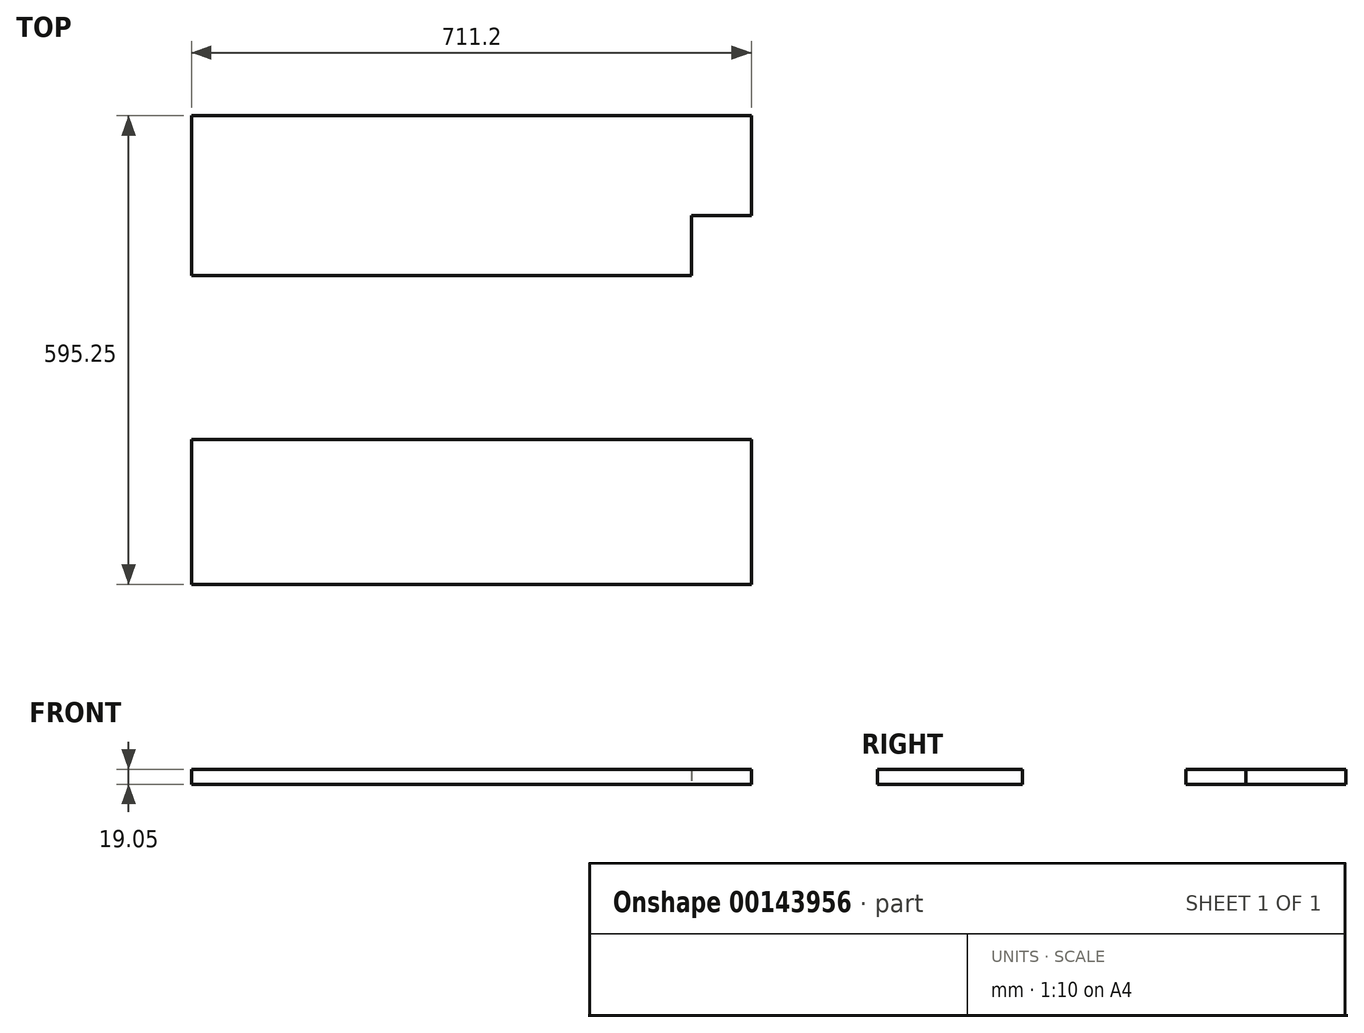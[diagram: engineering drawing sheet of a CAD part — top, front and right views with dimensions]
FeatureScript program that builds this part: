
annotation { "Feature Type Name" : "Feature", "Feature Type Description" : "" }
export const myFeature = defineFeature(function(context is Context, id is Id, definition is map)
    precondition{}
    {
        {
            var Q0;
            Q0=qCreatedBy(makeId("Top.planeOp"),FACE);
            var sketch = newSketch(context, id + "F0", { "sketchPlane" : qUnion([Q0])});
            skLineSegment(sketch, "E0.bottom", {"start": v(-183.98, 99.82) * mm, "end": v(527.22, 99.82) * mm});
            skLineSegment(sketch, "E0.top", {"start": v(-183.98, -103.38) * mm, "end": v(527.22, -103.38) * mm});
            skLineSegment(sketch, "E0.left", {"start": v(-183.98, 99.82) * mm, "end": v(-183.98, -103.38) * mm});
            skLineSegment(sketch, "E0.right", {"start": v(527.22, 99.82) * mm, "end": v(527.22, -103.38) * mm});
            skLineSegment(sketch, "E1", {"start": v(-234.36, 194.25) * mm, "end": v(600.55, 194.25) * mm, "construction": true});
            skLineSegment(sketch, "E2.MirrorCS", {"start": v(-183.98, 288.67) * mm, "end": v(-183.98, 491.87) * mm});
            skLineSegment(sketch, "E3.MirrorCS", {"start": v(-183.98, 288.67) * mm, "end": v(527.22, 288.67) * mm});
            skLineSegment(sketch, "E4.MirrorCS", {"start": v(527.22, 288.67) * mm, "end": v(527.22, 491.87) * mm});
            skLineSegment(sketch, "E5.MirrorCS", {"start": v(-183.98, 491.87) * mm, "end": v(527.22, 491.87) * mm});
            skLineSegment(sketch, "E6.bottom", {"start": v(451.02, 364.87) * mm, "end": v(527.22, 364.87) * mm});
            skLineSegment(sketch, "E6.top", {"start": v(451.02, 288.67) * mm, "end": v(527.22, 288.67) * mm});
            skLineSegment(sketch, "E6.left", {"start": v(451.02, 364.87) * mm, "end": v(451.02, 288.67) * mm});
            skLineSegment(sketch, "E6.right", {"start": v(527.22, 364.87) * mm, "end": v(527.22, 288.67) * mm});
            skSolve(sketch);
        }
        {
            var Q0;
            Q0=makeQuery(id+"F0.imprint","IMPRINT",FACE,{"disambiguationData":[TD([[makeQuery(id+"F0.imprint","IMPRINT",EDGE,{"derivedFrom":sQuery(id+"F0.wireOp",EDGE,"E0.bottom")}),-1.0]])]});
            extrude(context, id + "F1", {"entities" : qUnion([Q0]), "depth" : 19.05 * mm});
        }
        {
            var Q0;
            Q0=makeQuery(id+"F0.imprint","IMPRINT",FACE,{"disambiguationData":[TD([[makeQuery(id+"F0.imprint","IMPRINT",EDGE,{"derivedFrom":sQuery(id+"F0.wireOp",EDGE,"E2.MirrorCS")}),-1.0]])]});
            extrude(context, id + "F2", {"entities" : qUnion([Q0]), "depth" : 19.05 * mm});
        }
        {
            var Q0;
            Q0=makeQuery(id+"F0.imprint","IMPRINT",FACE,{"disambiguationData":[TD([[makeQuery(id+"F0.imprint","IMPRINT",EDGE,{"derivedFrom":sQuery(id+"F0.wireOp",EDGE,"E6.bottom")}),-1.0]])]});
            extrude(context, id + "F3", {"entities" : qUnion([Q0]), "depth" : 19.05 * mm});
        }
        {
            var Q0;
            Q0=makeQuery(id+"F1.opExtrude","CAP_FACE",FACE,{"disambiguationData":[OSD([sQuery(id+"F0.wireOp",EDGE,"E0.bottom"),sQuery(id+"F0.wireOp",EDGE,"E0.top"),sQuery(id+"F0.wireOp",EDGE,"E0.left"),sQuery(id+"F0.wireOp",EDGE,"E0.right")])],"isStart":false});
            var sketch = newSketch(context, id + "F4", { "sketchPlane" : qUnion([Q0])});
            skLineSegment(sketch, "E7.bottom", {"start": v(-183.98, 99.82) * mm, "end": v(527.22, 99.82) * mm});
            skLineSegment(sketch, "E7.top", {"start": v(-183.98, 80.77) * mm, "end": v(527.22, 80.77) * mm});
            skLineSegment(sketch, "E7.left", {"start": v(-183.98, 99.82) * mm, "end": v(-183.98, 80.77) * mm});
            skLineSegment(sketch, "E7.right", {"start": v(527.22, 99.82) * mm, "end": v(527.22, 80.77) * mm});
            skSolve(sketch);
        }
        {
            var Q0;
            Q0=makeQuery(id+"F4.imprint","IMPRINT",FACE,{"disambiguationData":[TD([[makeQuery(id+"F4.imprint","IMPRINT",EDGE,{"derivedFrom":sQuery(id+"F4.wireOp",EDGE,"E7.bottom")}),-1.0]])]});
            extrude(context, id + "F5", {"entities" : qUnion([Q0]), "operationType" : NewBodyOperationType.REMOVE, "endBound" : BoundingType.THROUGH_ALL, "oppositeDirection" : true, "depth" : 25.4 * mm});
        }
        {
            var Q0;
            Q0=makeQuery(id+"F3.opExtrude","SWEPT_BODY",BODY,{"disambiguationData":[OSD([sQuery(id+"F0.wireOp",EDGE,"E6.bottom"),sQuery(id+"F0.wireOp",EDGE,"E6.top"),sQuery(id+"F0.wireOp",EDGE,"E6.left"),sQuery(id+"F0.wireOp",EDGE,"E6.right")])]});
            deleteBodies(context, id + "F6", {"entities" : qUnion([Q0])});
        }
    });
